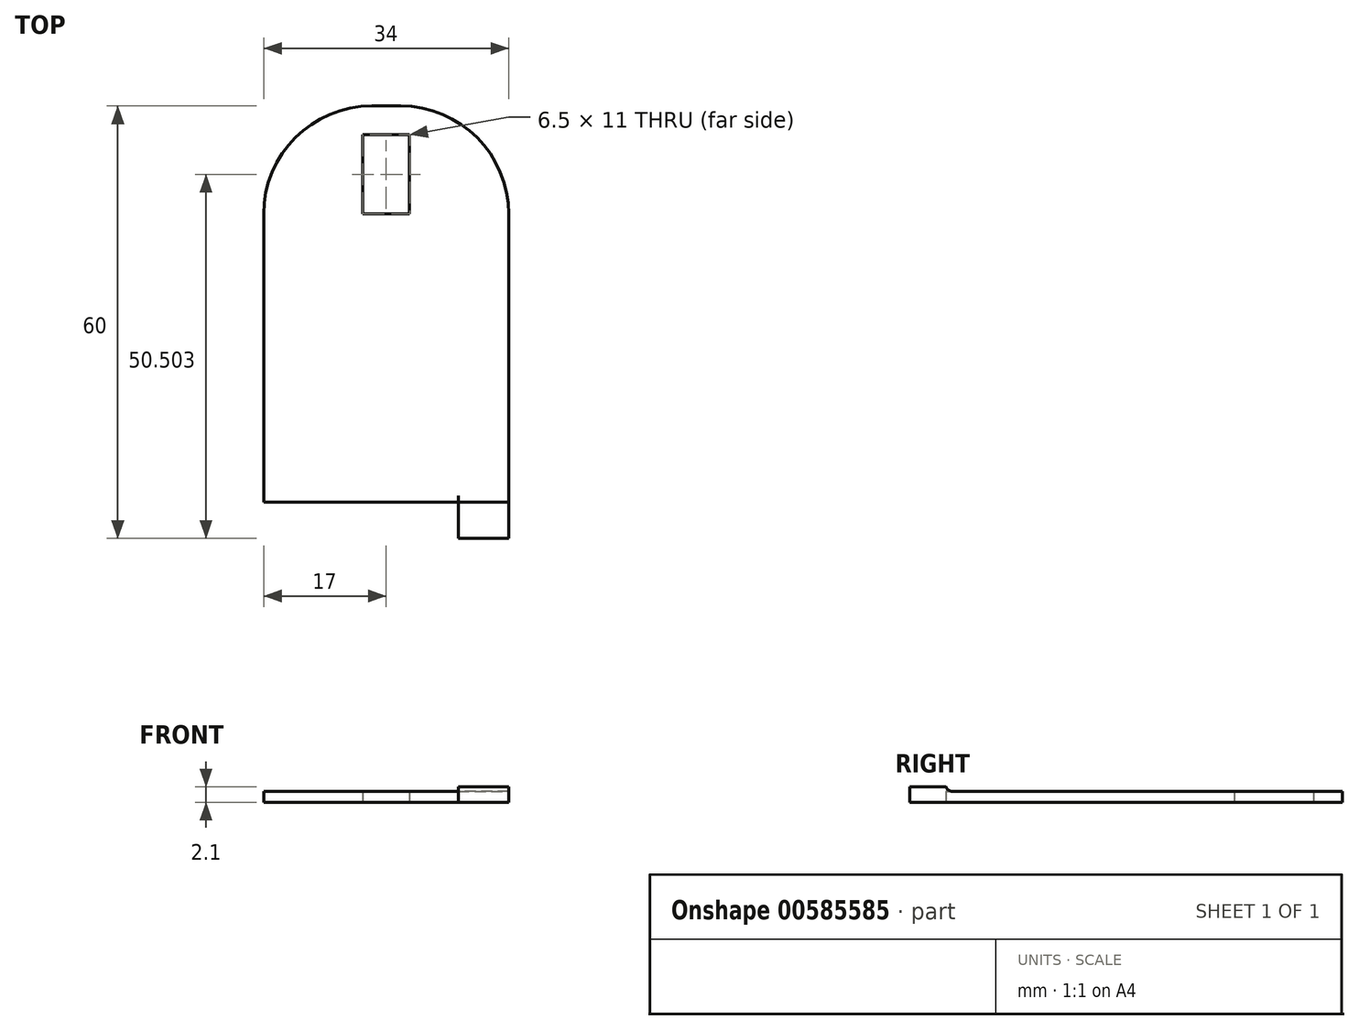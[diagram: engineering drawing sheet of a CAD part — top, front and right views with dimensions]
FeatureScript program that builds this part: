
annotation { "Feature Type Name" : "Feature", "Feature Type Description" : "" }
export const myFeature = defineFeature(function(context is Context, id is Id, definition is map)
    precondition{}
    {
        {
            var Q0;
            Q0=qCreatedBy(makeId("Top.planeOp"),FACE);
            var sketch = newSketch(context, id + "F0", { "sketchPlane" : qUnion([Q0])});
            skLineSegment(sketch, "E0.bottom", {"start": v(-17, 8.43) * mm, "end": v(0, 8.43) * mm});
            skLineSegment(sketch, "E0.top", {"start": v(-17, -46.57) * mm, "end": v(0, -46.57) * mm});
            skLineSegment(sketch, "E0.left", {"start": v(-17, 8.43) * mm, "end": v(-17, -46.57) * mm});
            skLineSegment(sketch, "E0.right", {"start": v(0, 8.43) * mm, "end": v(0, -46.57) * mm});
            skLineSegment(sketch, "E1.bottom", {"start": v(-17, -46.57) * mm, "end": v(-10, -46.57) * mm});
            skLineSegment(sketch, "E1.top", {"start": v(-17, -51.57) * mm, "end": v(-10, -51.57) * mm});
            skLineSegment(sketch, "E1.left", {"start": v(-17, -46.57) * mm, "end": v(-17, -51.57) * mm});
            skLineSegment(sketch, "E1.right", {"start": v(-10, -46.57) * mm, "end": v(-10, -51.57) * mm});
            skLineSegment(sketch, "E2.bottom", {"start": v(0, 4.43) * mm, "end": v(-3.25, 4.43) * mm});
            skLineSegment(sketch, "E2.top", {"start": v(0, -6.57) * mm, "end": v(-3.25, -6.57) * mm});
            skLineSegment(sketch, "E2.left", {"start": v(0, 4.43) * mm, "end": v(0, -6.57) * mm});
            skLineSegment(sketch, "E2.right", {"start": v(-3.25, 4.43) * mm, "end": v(-3.25, -6.57) * mm});
            skLineSegment(sketch, "E3.MirrorCS", {"start": v(17, 8.43) * mm, "end": v(0, 8.43) * mm});
            skLineSegment(sketch, "E4.MirrorCS", {"start": v(17, 8.43) * mm, "end": v(17, -46.57) * mm});
            skLineSegment(sketch, "E5.MirrorCS", {"start": v(0, 4.43) * mm, "end": v(3.25, 4.43) * mm});
            skLineSegment(sketch, "E6.MirrorCS", {"start": v(3.25, 4.43) * mm, "end": v(3.25, -6.57) * mm});
            skLineSegment(sketch, "E7.MirrorCS", {"start": v(0, -6.57) * mm, "end": v(3.25, -6.57) * mm});
            skLineSegment(sketch, "E8.MirrorCS", {"start": v(17, -46.57) * mm, "end": v(0, -46.57) * mm});
            skLineSegment(sketch, "E9.MirrorCS", {"start": v(10, -46.57) * mm, "end": v(10, -51.57) * mm});
            skLineSegment(sketch, "E10.MirrorCS", {"start": v(17, -46.57) * mm, "end": v(17, -51.57) * mm});
            skLineSegment(sketch, "E11.MirrorCS", {"start": v(17, -51.57) * mm, "end": v(10, -51.57) * mm});
            skSolve(sketch);
        }
        {
            var Q0;
            {var subQ1=sQuery(id+"F0.wireOp",EDGE,"E0.bottom");Q0=makeQuery(id+"F0.imprint","IMPRINT",FACE,{"disambiguationData":[TD([[makeQuery(id+"F0.imprint","IMPRINT",EDGE,{"derivedFrom":subQ1}),-1.0]])]});}
            var Q1;
            {var subQ1=sQuery(id+"F0.wireOp",EDGE,"E3.MirrorCS");Q1=makeQuery(id+"F0.imprint","IMPRINT",FACE,{"disambiguationData":[TD([[makeQuery(id+"F0.imprint","IMPRINT",EDGE,{"derivedFrom":subQ1}),1.0]])]});}
            var Q2;
            {var subQ2=sQuery(id+"F0.wireOp",EDGE,"E9.MirrorCS");Q2=makeQuery(id+"F0.imprint","IMPRINT",FACE,{"disambiguationData":[TD([[makeQuery(id+"F0.imprint","IMPRINT",EDGE,{"derivedFrom":subQ2}),1.0]])]});}
            var Q3;
            Q3=makeQuery(id+"F0.imprint","IMPRINT",FACE,{"disambiguationData":[TD([[makeQuery(id+"F0.imprint","IMPRINT",EDGE,{"derivedFrom":sQuery(id+"F0.wireOp",EDGE,"E1.bottom")}),-1.0]])]});
            extrude(context, id + "F1", {"entities" : qUnion([Q0, Q1, Q2, Q3]), "depth" : 1.5 * mm, "offsetDistance" : 25 * mm});
        }
        {
            var Q0;
            Q0=makeQuery(id+"F1.opExtrude","SWEPT_EDGE",EDGE,{"disambiguationData":[OSD([sQuery(id+"F0.wireOp",EDGE,"E3.MirrorCS"),sQuery(id+"F0.wireOp",EDGE,"E4.MirrorCS")])]});
            var Q1;
            Q1=makeQuery(id+"F1.opExtrude","SWEPT_EDGE",EDGE,{"disambiguationData":[OSD([sQuery(id+"F0.wireOp",EDGE,"E0.bottom"),sQuery(id+"F0.wireOp",EDGE,"E0.left")])]});
            fillet(context, id + "F2", {"entities" : qUnion([Q0, Q1]), "radius" : 15 * mm, "tangentPropagation" : true, "allowEdgeOverflow" : false});
        }
        {
            var Q0;
            {var subQ2=sQuery(id+"F0.wireOp",EDGE,"E9.MirrorCS");Q0=makeQuery(id+"F0.imprint","IMPRINT",FACE,{"disambiguationData":[TD([[makeQuery(id+"F0.imprint","IMPRINT",EDGE,{"derivedFrom":subQ2}),1.0]])]});}
            var Q1;
            Q1=makeQuery(id+"F0.imprint","IMPRINT",FACE,{"disambiguationData":[TD([[makeQuery(id+"F0.imprint","IMPRINT",EDGE,{"derivedFrom":sQuery(id+"F0.wireOp",EDGE,"E1.bottom")}),-1.0]])]});
            extrude(context, id + "F3", {"entities" : qUnion([Q0, Q1]), "operationType" : NewBodyOperationType.ADD, "depth" : 2.1 * mm, "offsetDistance" : 25 * mm});
        }
        {
            var Q0;
            Q0=makeQuery(id+"F3.boolean.opBoolean","INTERSECT",EDGE,{"derivedFrom":[makeQuery(id+"F1.opExtrude","CAP_FACE",FACE,{"disambiguationData":[OSD([sQuery(id+"F0.wireOp",EDGE,"E0.bottom"),sQuery(id+"F0.wireOp",EDGE,"E0.top"),sQuery(id+"F0.wireOp",EDGE,"E0.left"),sQuery(id+"F0.wireOp",EDGE,"E1.top"),sQuery(id+"F0.wireOp",EDGE,"E1.left"),sQuery(id+"F0.wireOp",EDGE,"E1.right"),sQuery(id+"F0.wireOp",EDGE,"E2.bottom"),sQuery(id+"F0.wireOp",EDGE,"E2.top"),sQuery(id+"F0.wireOp",EDGE,"E2.right"),sQuery(id+"F0.wireOp",EDGE,"E3.MirrorCS"),sQuery(id+"F0.wireOp",EDGE,"E4.MirrorCS"),sQuery(id+"F0.wireOp",EDGE,"E5.MirrorCS"),sQuery(id+"F0.wireOp",EDGE,"E6.MirrorCS"),sQuery(id+"F0.wireOp",EDGE,"E7.MirrorCS"),sQuery(id+"F0.wireOp",EDGE,"E8.MirrorCS"),sQuery(id+"F0.wireOp",EDGE,"E9.MirrorCS"),sQuery(id+"F0.wireOp",EDGE,"E10.MirrorCS"),sQuery(id+"F0.wireOp",EDGE,"E11.MirrorCS")])],"isStart":false}),makeQuery(id+"F3.opExtrude","SWEPT_FACE",FACE,{"disambiguationData":[OSD([sQuery(id+"F0.wireOp",EDGE,"E1.bottom")])]})]});
            var Q1;
            {var subQ0=sQuery(id+"F0.wireOp",EDGE,"E8.MirrorCS");Q1=makeQuery(id+"F3.boolean.opBoolean","INTERSECT",EDGE,{"derivedFrom":[makeQuery(id+"F1.opExtrude","CAP_FACE",FACE,{"disambiguationData":[OSD([sQuery(id+"F0.wireOp",EDGE,"E0.bottom"),sQuery(id+"F0.wireOp",EDGE,"E0.top"),sQuery(id+"F0.wireOp",EDGE,"E0.left"),sQuery(id+"F0.wireOp",EDGE,"E1.top"),sQuery(id+"F0.wireOp",EDGE,"E1.left"),sQuery(id+"F0.wireOp",EDGE,"E1.right"),sQuery(id+"F0.wireOp",EDGE,"E2.bottom"),sQuery(id+"F0.wireOp",EDGE,"E2.top"),sQuery(id+"F0.wireOp",EDGE,"E2.right"),sQuery(id+"F0.wireOp",EDGE,"E3.MirrorCS"),sQuery(id+"F0.wireOp",EDGE,"E4.MirrorCS"),sQuery(id+"F0.wireOp",EDGE,"E5.MirrorCS"),sQuery(id+"F0.wireOp",EDGE,"E6.MirrorCS"),sQuery(id+"F0.wireOp",EDGE,"E7.MirrorCS"),subQ0,sQuery(id+"F0.wireOp",EDGE,"E9.MirrorCS"),sQuery(id+"F0.wireOp",EDGE,"E10.MirrorCS"),sQuery(id+"F0.wireOp",EDGE,"E11.MirrorCS")])],"isStart":false}),makeQuery(id+"F3.opExtrude","SWEPT_FACE",FACE,{"disambiguationData":[OSD([subQ0])]})]});}
            fillet(context, id + "F4", {"entities" : qUnion([Q0, Q1]), "radius" : 1 * mm, "tangentPropagation" : true, "allowEdgeOverflow" : false});
        }
    });
